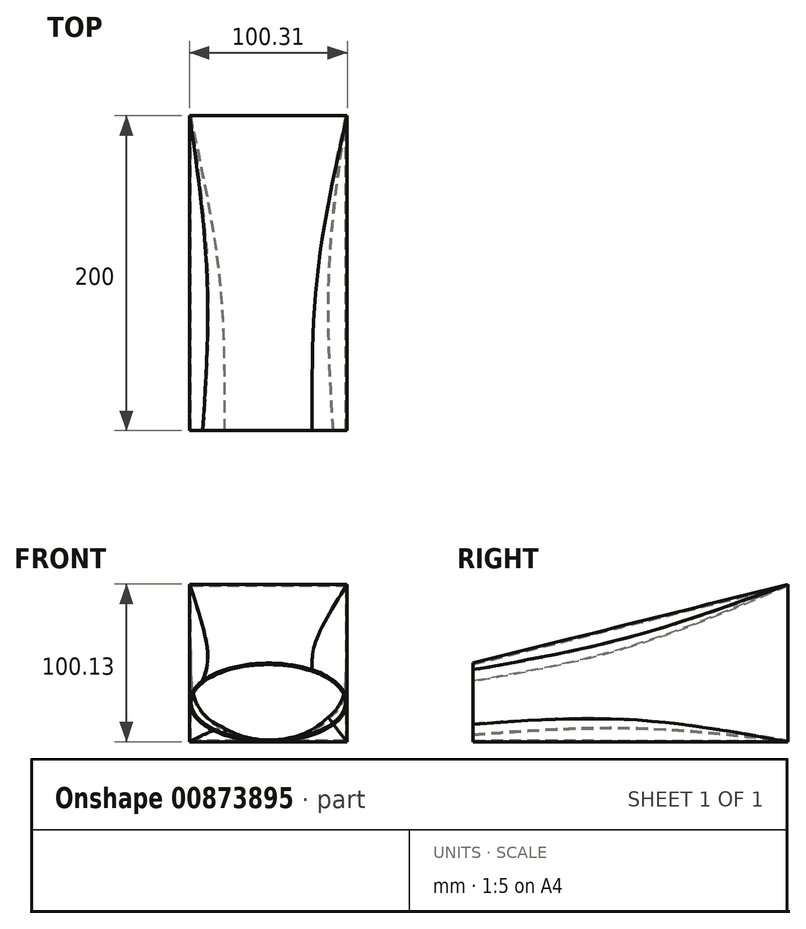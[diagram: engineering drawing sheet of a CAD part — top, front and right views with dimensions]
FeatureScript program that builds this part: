
annotation { "Feature Type Name" : "Feature", "Feature Type Description" : "" }
export const myFeature = defineFeature(function(context is Context, id is Id, definition is map)
    precondition{}
    {
        {
            var Q0;
            Q0=qCreatedBy(makeId("Front.planeOp"),FACE);
            var sketch = newSketch(context, id + "F0", { "sketchPlane" : qUnion([Q0])});
            skLineSegment(sketch, "E0.bottom", {"start": v(50, -50) * mm, "end": v(-50, -50) * mm});
            skLineSegment(sketch, "E0.top", {"start": v(50, 50) * mm, "end": v(-50, 50) * mm});
            skLineSegment(sketch, "E0.left", {"start": v(50, -50) * mm, "end": v(50, 50) * mm});
            skLineSegment(sketch, "E0.right", {"start": v(-50, -50) * mm, "end": v(-50, 50) * mm});
            skPoint(sketch, "E0.middle", {"position": v(0, 0) * mm});
            skSolve(sketch);
        }
        {
            var Q0;
            Q0=qCreatedBy(makeId("Front.planeOp"),FACE);
            cPlane(context, id + "F1", {"entities" : qUnion([Q0]), "cplaneType" : CPlaneType.OFFSET, "offset" : 200 * mm, "width" : 150 * mm, "height" : 150 * mm});
        }
        {
            var Q0;
            Q0=qCreatedBy(id+"F1.planeOp",FACE);
            var sketch = newSketch(context, id + "F2", { "sketchPlane" : qUnion([Q0])});
            skPoint(sketch, "E1.0", {"position": v(-50, 50) * mm});
            skPoint(sketch, "E2.0", {"position": v(50, 50) * mm});
            skPoint(sketch, "E3.0", {"position": v(50, -50) * mm});
            skPoint(sketch, "E4.0", {"position": v(-50, -50) * mm});
            skPoint(sketch, "E5.0", {"position": v(-50, 0) * mm});
            skPoint(sketch, "E6.0", {"position": v(50, 0) * mm});
            skPoint(sketch, "E7.0", {"position": v(0, 50) * mm});
            skPoint(sketch, "E8.0", {"position": v(0, -50) * mm});
            skLineSegment(sketch, "E9", {"start": v(0, -50) * mm, "end": v(0, 0) * mm, "construction": true});
            skEllipse(sketch, "E10", {"center": v(0, -25) * mm, "majorRadius": 50 * mm, "minorRadius": 25 * mm, "majorAxis": v(1, 0)});
            skSolve(sketch);
        }
        {
            var Q0;
            Q0=qCreatedBy(makeId("Front.planeOp"),FACE);
            cPlane(context, id + "F3", {"entities" : qUnion([Q0]), "cplaneType" : CPlaneType.OFFSET, "offset" : 100 * mm, "width" : 150 * mm, "height" : 150 * mm});
        }
        {
            var Q0;
            Q0=qCreatedBy(id+"F3.planeOp",FACE);
            var sketch = newSketch(context, id + "F4", { "sketchPlane" : qUnion([Q0])});
            skLineSegment(sketch, "E11.0.0", {"start": v(50, -50) * mm, "end": v(50, 50) * mm, "construction": true});
            skLineSegment(sketch, "E11.0.1", {"start": v(50, 50) * mm, "end": v(-50, 50) * mm, "construction": true});
            skLineSegment(sketch, "E11.0.2", {"start": v(-50, 50) * mm, "end": v(-50, -50) * mm, "construction": true});
            skLineSegment(sketch, "E11.0.3", {"start": v(-50, -50) * mm, "end": v(50, -50) * mm, "construction": true});
            skEllipse(sketch, "E12.0.0", {"center": v(0, -25) * mm, "majorRadius": 50 * mm, "minorRadius": 25 * mm, "majorAxis": v(1, 0), "construction": true});
            skLineSegment(sketch, "E13", {"start": v(0, -25) * mm, "end": v(0, 0) * mm, "construction": true});
            skEllipse(sketch, "E14", {"center": v(0, -12.5) * mm, "majorRadius": 50 * mm, "minorRadius": 37.5 * mm, "majorAxis": v(1, 0)});
            skSolve(sketch);
        }
        {
            var Q0;
            Q0=makeQuery(id+"F2.imprint","IMPRINT",FACE,{"disambiguationData":[TD([[makeQuery(id+"F2.imprint","IMPRINT",EDGE,{"derivedFrom":sQuery(id+"F2.wireOp",EDGE,"E10")}),1.0]])]});
            var Q1;
            Q1=makeQuery(id+"F4.imprint","IMPRINT",FACE,{"disambiguationData":[TD([[makeQuery(id+"F4.imprint","IMPRINT",EDGE,{"derivedFrom":sQuery(id+"F4.wireOp",EDGE,"E14")}),1.0]])]});
            var Q2;
            Q2=makeQuery(id+"F0.imprint","IMPRINT",FACE,{"disambiguationData":[TD([[makeQuery(id+"F0.imprint","IMPRINT",EDGE,{"derivedFrom":sQuery(id+"F0.wireOp",EDGE,"E0.bottom")}),-1.0]])]});
            loft(context, id + "F5", {"sheetProfilesArray" : [{ "sheetProfileEntities" : qUnion([Q0]) }, { "sheetProfileEntities" : qUnion([Q1]) }, { "sheetProfileEntities" : qUnion([Q2]) }]});
        }
        {
            var Q0;
            Q0=makeQuery(id+"F5.opLoft","CAP_FACE",FACE,{"disambiguationData":[OSD([makeQuery(id+"F2.imprint","IMPRINT",FACE,{"disambiguationData":[TD([[makeQuery(id+"F2.imprint","IMPRINT",EDGE,{"derivedFrom":sQuery(id+"F2.wireOp",EDGE,"E10")}),1.0]])]})])],"isStart":true});
            var Q1;
            Q1=makeQuery(id+"F5.opLoft","CAP_FACE",FACE,{"disambiguationData":[OSD([makeQuery(id+"F0.imprint","IMPRINT",FACE,{"disambiguationData":[TD([[makeQuery(id+"F0.imprint","IMPRINT",EDGE,{"derivedFrom":sQuery(id+"F0.wireOp",EDGE,"E0.bottom")}),-1.0]])]})])],"isStart":true});
            shell(context, id + "F6", {"entities" : qUnion([Q0, Q1]), "thickness" : 1 * mm});
        }
    });
